# Revit family: HERZ-Thermostatkopf M28x1.5 7260
name_source: partatom
category: Rohrzubehör
units: mm (PartAtom-declared; Revit-internal decimal feet)

## family parameters
Arbeitsebenenbasiert = Nein
Beim Laden mit Abzugskörper schneiden = Nein
Bemaßung runder Anschluss = Durchmesser verwenden
Gemeinsam genutzt = Nein
Immer vertikal = Nein
OmniClass-Nummer = 23.65.55.14
OmniClass-Titel = Valves for Liquid Services
Teiletyp = Normal

## types (1)
- HERZ-Thermostatkopf M28x1.5 7260
    Anwendung = Zur Montage auf allen HERZ-Ventilen, die für thermostatischen Betrieb eingerichtet sind.
    Ausführungen = Heizkörperthermostat mit Flüssigkeitsfühler (Hydrosensor)
mit automatischer Frostsicherung und Begrenzung ud Blockierung des Sollwertbereiches. Handradfarbe weiß.
    Bestellnummer = 1726006
    Funktionsweise = Der HERZ-Thermostat dient als Fühl- und Regelelement.
Durch die Volumsänderung der Flüssigkeitsfüllung im HERZ-Hydrosensor wird die Schubspindel des Ventils bewegt.
    H01 = 45.8 mm  [stored 0.150262 ft]
    H02 = 20.5 mm  [stored 0.0672572 ft]
    H03 = 4.5 mm  [stored 0.0147638 ft]
    H04 = 11.7 mm
    H05 = 10.5 mm  [stored 0.0344488 ft]
    H06 = 3.5 mm  [stored 0.0114829 ft]
    H07 = 59 mm
    H08 = 10 mm  [stored 0.0328084 ft]
    H09 = 3.5 mm  [stored 0.0114829 ft]
    Handrad = Kunststoff, weiß
    Hersteller = HERZ Armaturen Ges.m.b.H.
    R01 = 22.4 mm  [stored 0.0734908 ft]
    R02 = 12.2 mm
    R03 = 13.2 mm
    R04 = 14.75 mm
    R05 = 16.35 mm  [stored 0.0536417 ft]
    R06 = 24 mm  [stored 0.0787402 ft]
    R07 = 6 mm  [stored 0.019685 ft]
    R08 = 15 mm  [stored 0.0492126 ft]
    S01 = 79.5 mm  [stored 0.260827 ft]
    S02 = 60 mm  [stored 0.19685 ft]
    Sollwerbereich = 6 - 28°C
    URL = www.herz-armaturen.at
    Vorgabe-Ansicht = 0 mm  [stored 0 ft]
    W01 = 135.00°
    W02 = 120.00°
    automatische Frostsicherung = bei ca. 6°C

note: [stored X ft] marks values corroborated as IEEE doubles in the binary element streams (Revit-internal decimal feet)
